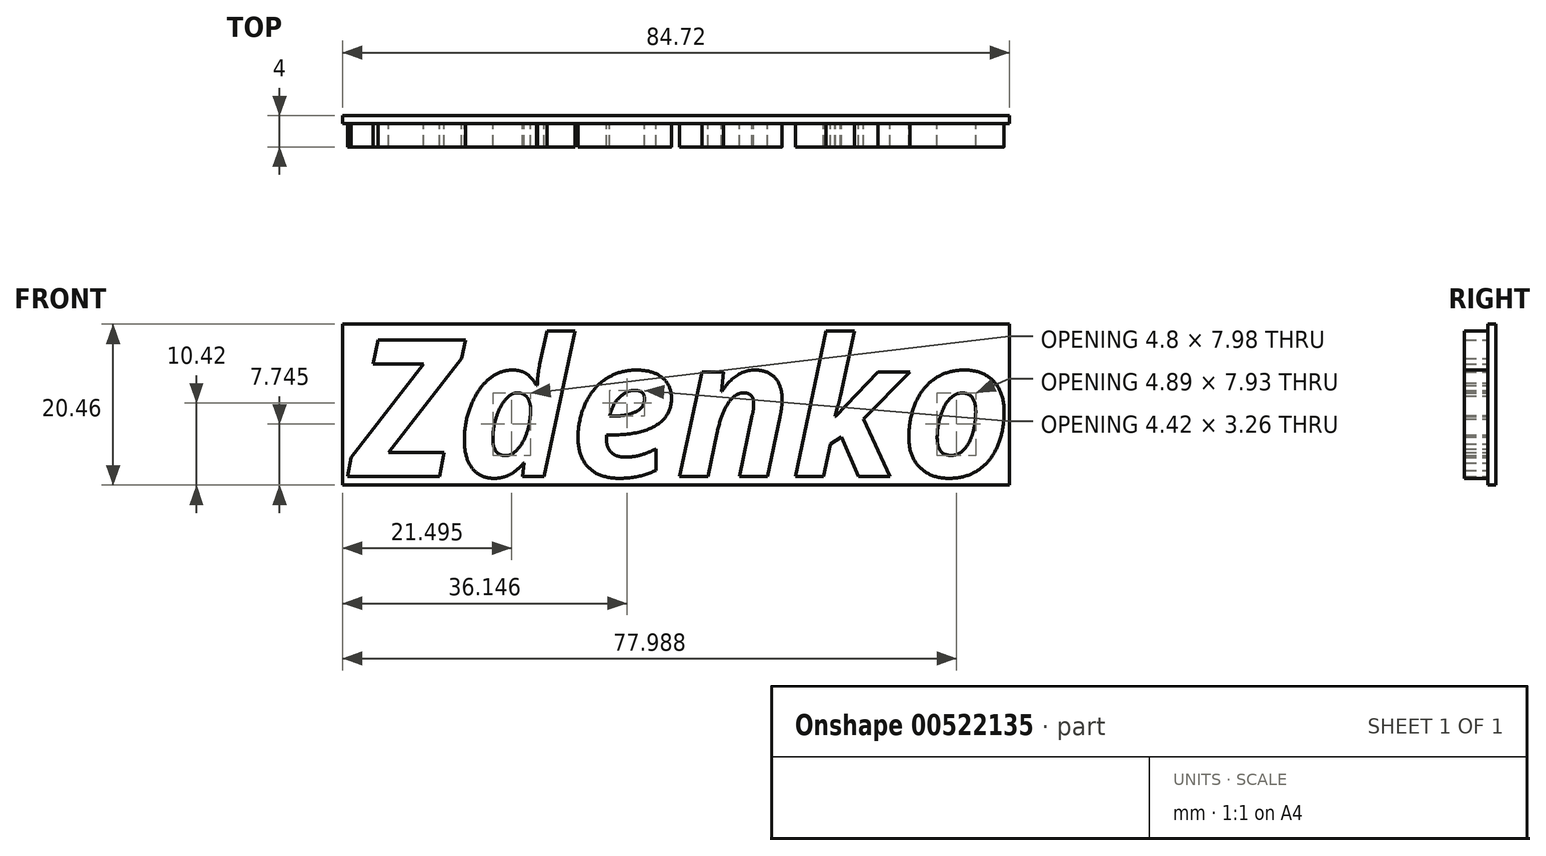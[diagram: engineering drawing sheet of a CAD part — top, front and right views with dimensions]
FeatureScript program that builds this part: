
annotation { "Feature Type Name" : "Feature", "Feature Type Description" : "" }
export const myFeature = defineFeature(function(context is Context, id is Id, definition is map)
    precondition{}
    {
        {
            var Q0;
            Q0=qCreatedBy(makeId("Front.planeOp"),FACE);
            var sketch = newSketch(context, id + "F0", { "sketchPlane" : qUnion([Q0])});
            skText(sketch, "E0", { "text": "Zdenko", "fontName": "OpenSans-BoldItalic.ttf"});
            const initialGuessF0  = {"E0": [-0.04475, -0.00012, 1, 0, 0.0175]};
            skSetInitialGuess(sketch, initialGuessF0);
            skSolve(sketch);
        }
        {
            var Q0;
            Q0=qSketchRegion(id+"F0",true);
            extrude(context, id + "F1", {"entities" : qUnion([Q0]), "depth" : 3 * mm});
        }
        {
            var Q0;
            Q0=makeQuery(id+"F0.imprint","IMPRINT",FACE,{"disambiguationData":[TD([[makeQuery(id+"F0.imprint","IMPRINT",EDGE,{"derivedFrom":sQuery(id+"F0.wireOp",EDGE,"E0.sketch_text.stroke-36")}),-1.0]])]});
            var sketch = newSketch(context, id + "F2", { "sketchPlane" : qUnion([Q0])});
            skLineSegment(sketch, "E1.bottom", {"start": v(-46.13, 19.23) * mm, "end": v(38.6, 19.23) * mm});
            skLineSegment(sketch, "E1.top", {"start": v(-46.13, -1.23) * mm, "end": v(38.6, -1.23) * mm});
            skLineSegment(sketch, "E1.left", {"start": v(-46.13, 19.23) * mm, "end": v(-46.13, -1.23) * mm});
            skLineSegment(sketch, "E1.right", {"start": v(38.6, 19.23) * mm, "end": v(38.6, -1.23) * mm});
            skSolve(sketch);
        }
        {
            var Q0;
            Q0=qSketchRegion(id+"F2",true);
            extrude(context, id + "F3", {"entities" : qUnion([Q0]), "oppositeDirection" : true, "depth" : 1 * mm, "offsetDistance" : 25 * mm});
        }
    });
